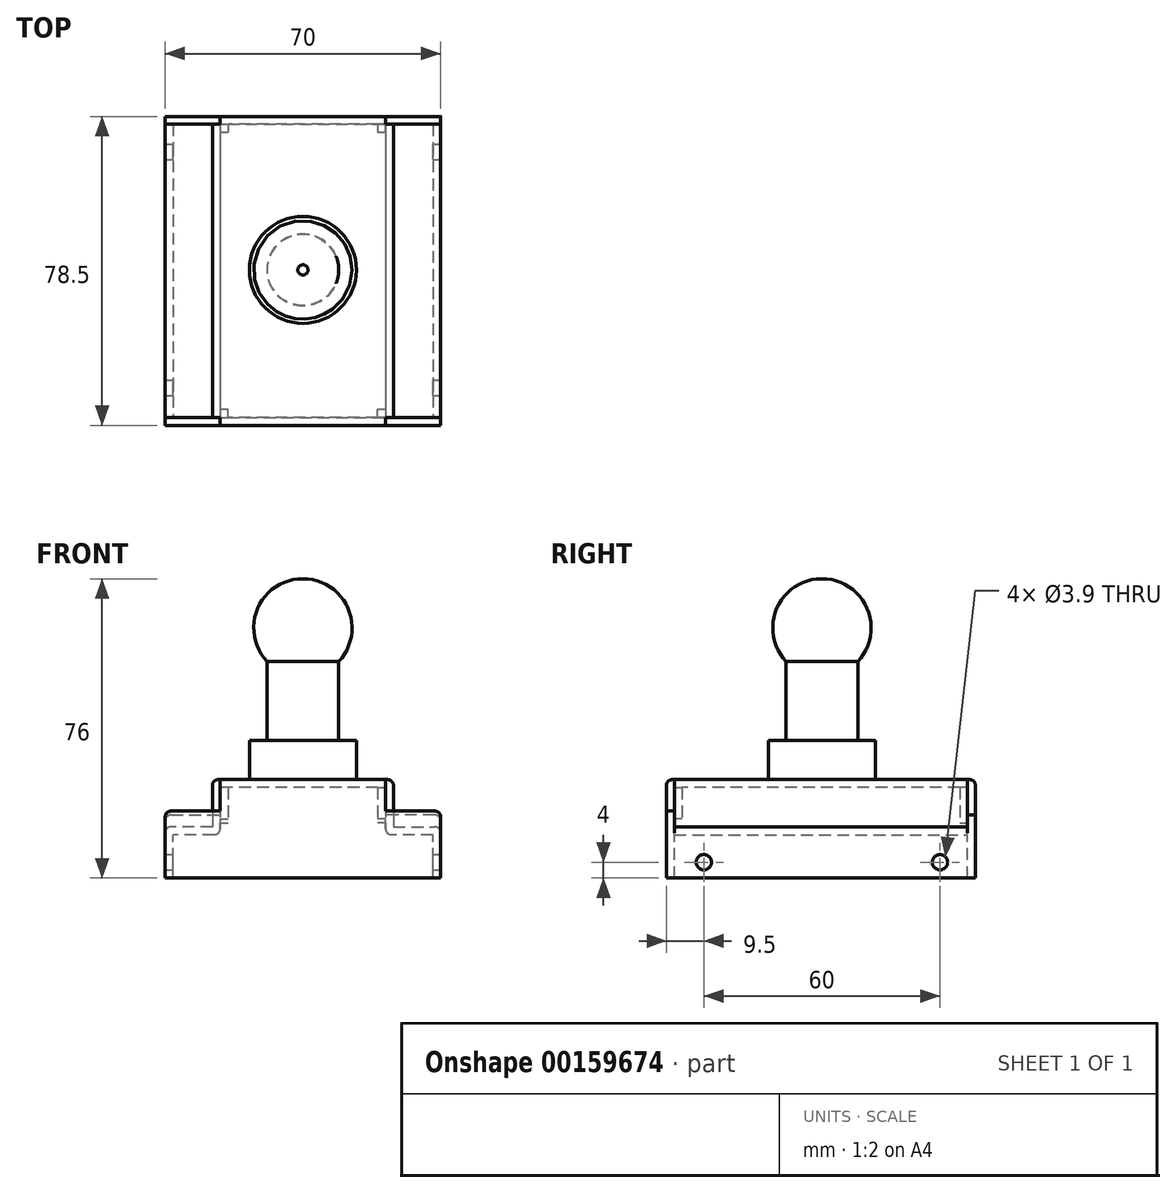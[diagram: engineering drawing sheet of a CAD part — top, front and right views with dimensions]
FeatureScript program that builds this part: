
annotation { "Feature Type Name" : "Feature", "Feature Type Description" : "" }
export const myFeature = defineFeature(function(context is Context, id is Id, definition is map)
    precondition{}
    {
        {
            var Q0;
            Q0=qCreatedBy(makeId("Front.planeOp"),FACE);
            cPlane(context, id + "F0", {"entities" : qUnion([Q0]), "cplaneType" : CPlaneType.OFFSET, "offset" : 39.5 * mm, "width" : 150 * mm, "height" : 150 * mm});
        }
        {
            var Q0;
            Q0=qCreatedBy(id+"F0.planeOp",FACE);
            var sketch = newSketch(context, id + "F1", { "sketchPlane" : qUnion([Q0])});
            skLineSegment(sketch, "E0.bottom", {"start": v(-35, 0) * mm, "end": v(35, 0) * mm});
            skLineSegment(sketch, "E0.top", {"start": v(-35, 25) * mm, "end": v(35, 25) * mm});
            skLineSegment(sketch, "E0.left", {"start": v(-35, 0) * mm, "end": v(-35, 25) * mm});
            skLineSegment(sketch, "E0.right", {"start": v(35, 0) * mm, "end": v(35, 25) * mm});
            skSolve(sketch);
        }
        {
            var Q0;
            Q0 = qSketchRegion(id + "F1", true);
            extrude(context, id + "F2", {"entities" : qUnion([Q0]), "oppositeDirection" : true, "depth" : 78.5 * mm});
        }
        {
            var Q0;
            Q0=makeQuery(id+"F2.opExtrude","CAP_FACE",FACE,{"disambiguationData":[OSD([sQuery(id+"F1.wireOp",EDGE,"E0.bottom"),sQuery(id+"F1.wireOp",EDGE,"E0.top"),sQuery(id+"F1.wireOp",EDGE,"E0.left"),sQuery(id+"F1.wireOp",EDGE,"E0.right")])],"isStart":true});
            var sketch = newSketch(context, id + "F3", { "sketchPlane" : qUnion([Q0])});
            skLineSegment(sketch, "E1.bottom", {"start": v(-36, 27) * mm, "end": v(-21, 27) * mm});
            skLineSegment(sketch, "E1.top", {"start": v(-36, 17) * mm, "end": v(-21, 17) * mm});
            skLineSegment(sketch, "E1.left", {"start": v(-36, 27) * mm, "end": v(-36, 17) * mm});
            skLineSegment(sketch, "E1.right", {"start": v(-21, 27) * mm, "end": v(-21, 17) * mm});
            skLineSegment(sketch, "E2.MirrorCS", {"start": v(36, 27) * mm, "end": v(21, 27) * mm});
            skLineSegment(sketch, "E3.MirrorCS", {"start": v(21, 27) * mm, "end": v(21, 17) * mm});
            skLineSegment(sketch, "E4.MirrorCS", {"start": v(36, 17) * mm, "end": v(21, 17) * mm});
            skLineSegment(sketch, "E5.MirrorCS", {"start": v(36, 27) * mm, "end": v(36, 17) * mm});
            skSolve(sketch);
        }
        {
            var Q0;
            Q0 = qSketchRegion(id + "F3", true);
            extrude(context, id + "F4", {"entities" : qUnion([Q0]), "operationType" : NewBodyOperationType.REMOVE, "oppositeDirection" : true, "depth" : 2 * mm});
        }
        {
            var Q0;
            Q0=makeQuery(id+"F2.opExtrude","CAP_FACE",FACE,{"disambiguationData":[OSD([sQuery(id+"F1.wireOp",EDGE,"E0.bottom"),sQuery(id+"F1.wireOp",EDGE,"E0.top"),sQuery(id+"F1.wireOp",EDGE,"E0.left"),sQuery(id+"F1.wireOp",EDGE,"E0.right")])],"isStart":false});
            var sketch = newSketch(context, id + "F5", { "sketchPlane" : qUnion([Q0])});
            skLineSegment(sketch, "E6.bottom", {"start": v(-36, 26) * mm, "end": v(-21, 26) * mm});
            skLineSegment(sketch, "E6.top", {"start": v(-36, 16) * mm, "end": v(-21, 16) * mm});
            skLineSegment(sketch, "E6.left", {"start": v(-36, 26) * mm, "end": v(-36, 16) * mm});
            skLineSegment(sketch, "E6.right", {"start": v(-21, 26) * mm, "end": v(-21, 16) * mm});
            skLineSegment(sketch, "E7.MirrorCS", {"start": v(36, 26) * mm, "end": v(21, 26) * mm});
            skLineSegment(sketch, "E8.MirrorCS", {"start": v(36, 16) * mm, "end": v(21, 16) * mm});
            skLineSegment(sketch, "E9.MirrorCS", {"start": v(21, 26) * mm, "end": v(21, 16) * mm});
            skLineSegment(sketch, "E10.MirrorCS", {"start": v(36, 26) * mm, "end": v(36, 16) * mm});
            skSolve(sketch);
        }
        {
            var Q0;
            Q0 = qSketchRegion(id + "F5", true);
            extrude(context, id + "F6", {"entities" : qUnion([Q0]), "operationType" : NewBodyOperationType.REMOVE, "oppositeDirection" : true, "depth" : 2 * mm});
        }
        {
            var Q0;
            Q0=makeQuery(id+"F4.boolean.opBoolean","COPY",FACE,{"derivedFrom":makeQuery(id+"F4.opExtrude","CAP_FACE",FACE,{"disambiguationData":[OSD([sQuery(id+"F3.wireOp",EDGE,"E2.MirrorCS"),sQuery(id+"F3.wireOp",EDGE,"E3.MirrorCS"),sQuery(id+"F3.wireOp",EDGE,"E4.MirrorCS"),sQuery(id+"F3.wireOp",EDGE,"E5.MirrorCS")])],"isStart":false})});
            var sketch = newSketch(context, id + "F7", { "sketchPlane" : qUnion([Q0])});
            skLineSegment(sketch, "E11.bottom", {"start": v(-23, 32.24) * mm, "end": v(-40.46, 32.24) * mm});
            skLineSegment(sketch, "E11.top", {"start": v(-23, 13) * mm, "end": v(-40.46, 13) * mm});
            skLineSegment(sketch, "E11.left", {"start": v(-23, 32.24) * mm, "end": v(-23, 13) * mm});
            skLineSegment(sketch, "E11.right", {"start": v(-40.46, 32.24) * mm, "end": v(-40.46, 13) * mm});
            skLineSegment(sketch, "E12.MirrorCS", {"start": v(23, 32.24) * mm, "end": v(23, 13) * mm});
            skLineSegment(sketch, "E13.MirrorCS", {"start": v(23, 32.24) * mm, "end": v(40.46, 32.24) * mm});
            skLineSegment(sketch, "E14.MirrorCS", {"start": v(40.46, 32.24) * mm, "end": v(40.46, 13) * mm});
            skLineSegment(sketch, "E15.MirrorCS", {"start": v(23, 13) * mm, "end": v(40.46, 13) * mm});
            skSolve(sketch);
        }
        {
            var Q0;
            Q0 = qSketchRegion(id + "F7", true);
            extrude(context, id + "F8", {"entities" : qUnion([Q0]), "operationType" : NewBodyOperationType.REMOVE, "oppositeDirection" : true, "depth" : 74.5 * mm});
        }
        {
            var Q0;
            Q0=makeQuery(id+"F2.opExtrude","CAP_EDGE",EDGE,{"disambiguationData":[OSD([sQuery(id+"F1.wireOp",EDGE,"E0.top")])],"isStart":true});
            var Q1;
            Q1=makeQuery(id+"F8.boolean.opBoolean","INTERSECT",EDGE,{"derivedFrom":[makeQuery(id+"F2.opExtrude","SWEPT_FACE",FACE,{"disambiguationData":[OSD([sQuery(id+"F1.wireOp",EDGE,"E0.top")])]}),makeQuery(id+"F8.opExtrude","SWEPT_FACE",FACE,{"disambiguationData":[OSD([sQuery(id+"F7.wireOp",EDGE,"E12.MirrorCS")])]})]});
            var Q2;
            Q2=makeQuery(id+"F2.opExtrude","CAP_EDGE",EDGE,{"disambiguationData":[OSD([sQuery(id+"F1.wireOp",EDGE,"E0.top")])],"isStart":false});
            var Q3;
            Q3=makeQuery(id+"F8.boolean.opBoolean","INTERSECT",EDGE,{"derivedFrom":[makeQuery(id+"F2.opExtrude","SWEPT_FACE",FACE,{"disambiguationData":[OSD([sQuery(id+"F1.wireOp",EDGE,"E0.top")])]}),makeQuery(id+"F8.opExtrude","SWEPT_FACE",FACE,{"disambiguationData":[OSD([sQuery(id+"F7.wireOp",EDGE,"E11.left")])]})]});
            var Q4;
            Q4=makeQuery(id+"F6.boolean.opBoolean","INTERSECT",EDGE,{"derivedFrom":[makeQuery(id+"F2.opExtrude","SWEPT_FACE",FACE,{"disambiguationData":[OSD([sQuery(id+"F1.wireOp",EDGE,"E0.left")])]}),makeQuery(id+"F6.opExtrude","SWEPT_FACE",FACE,{"disambiguationData":[OSD([sQuery(id+"F5.wireOp",EDGE,"E8.MirrorCS")])]})]});
            var Q5;
            Q5=makeQuery(id+"F6.boolean.opBoolean","INTERSECT",EDGE,{"derivedFrom":[makeQuery(id+"F2.opExtrude","SWEPT_FACE",FACE,{"disambiguationData":[OSD([sQuery(id+"F1.wireOp",EDGE,"E0.right")])]}),makeQuery(id+"F6.opExtrude","SWEPT_FACE",FACE,{"disambiguationData":[OSD([sQuery(id+"F5.wireOp",EDGE,"E6.top")])]})]});
            var Q6;
            Q6=makeQuery(id+"F4.boolean.opBoolean","INTERSECT",EDGE,{"derivedFrom":[makeQuery(id+"F2.opExtrude","SWEPT_FACE",FACE,{"disambiguationData":[OSD([sQuery(id+"F1.wireOp",EDGE,"E0.right")])]}),makeQuery(id+"F4.opExtrude","SWEPT_FACE",FACE,{"disambiguationData":[OSD([sQuery(id+"F3.wireOp",EDGE,"E4.MirrorCS")])]})]});
            var Q7;
            Q7=makeQuery(id+"F4.boolean.opBoolean","INTERSECT",EDGE,{"derivedFrom":[makeQuery(id+"F2.opExtrude","SWEPT_FACE",FACE,{"disambiguationData":[OSD([sQuery(id+"F1.wireOp",EDGE,"E0.left")])]}),makeQuery(id+"F4.opExtrude","SWEPT_FACE",FACE,{"disambiguationData":[OSD([sQuery(id+"F3.wireOp",EDGE,"E1.top")])]})]});
            var Q8;
            Q8=makeQuery(id+"F8.boolean.opBoolean","INTERSECT",EDGE,{"derivedFrom":[makeQuery(id+"F2.opExtrude","SWEPT_FACE",FACE,{"disambiguationData":[OSD([sQuery(id+"F1.wireOp",EDGE,"E0.left")])]}),makeQuery(id+"F8.opExtrude","SWEPT_FACE",FACE,{"disambiguationData":[OSD([sQuery(id+"F7.wireOp",EDGE,"E11.top")])]})]});
            var Q9;
            Q9=makeQuery(id+"F8.boolean.opBoolean","INTERSECT",EDGE,{"derivedFrom":[makeQuery(id+"F2.opExtrude","SWEPT_FACE",FACE,{"disambiguationData":[OSD([sQuery(id+"F1.wireOp",EDGE,"E0.right")])]}),makeQuery(id+"F8.opExtrude","SWEPT_FACE",FACE,{"disambiguationData":[OSD([sQuery(id+"F7.wireOp",EDGE,"E15.MirrorCS")])]})]});
            fillet(context, id + "F9", {"entities" : qUnion([Q0, Q1, Q2, Q3, Q4, Q5, Q6, Q7, Q8, Q9]), "radius" : 1.5 * mm, "tangentPropagation" : true, "allowEdgeOverflow" : false});
        }
        {
            var Q0;
            Q0=makeQuery(id+"F2.opExtrude","SWEPT_FACE",FACE,{"disambiguationData":[OSD([sQuery(id+"F1.wireOp",EDGE,"E0.bottom")])]});
            shell(context, id + "F10", {"entities" : qUnion([Q0]), "thickness" : 2 * mm});
        }
        {
            var Q0;
            Q0=makeQuery(id+"F10.opShell","OFFSET_EDGE",EDGE,{"disambiguationData":[OSD([sQuery(id+"F7.wireOp",EDGE,"E12.MirrorCS"),sQuery(id+"F7.wireOp",EDGE,"E15.MirrorCS")])]});
            var Q1;
            Q1=makeQuery(id+"F10.opShell","OFFSET_EDGE",EDGE,{"disambiguationData":[OSD([sQuery(id+"F7.wireOp",EDGE,"E11.top"),sQuery(id+"F7.wireOp",EDGE,"E11.left")])]});
            fillet(context, id + "F11", {"entities" : qUnion([Q0, Q1]), "radius" : 1.5 * mm, "tangentPropagation" : true, "allowEdgeOverflow" : false});
        }
        {
            var Q0;
            Q0=makeQuery(id+"F2.opExtrude","SWEPT_FACE",FACE,{"disambiguationData":[OSD([sQuery(id+"F1.wireOp",EDGE,"E0.right")])]});
            var sketch = newSketch(context, id + "F12", { "sketchPlane" : qUnion([Q0])});
            skCircle(sketch, "E16", {"center": v(-30, 4) * mm, "radius": 1.95 * mm});
            skCircle(sketch, "E17.MirrorC", {"center": v(30, 4) * mm, "radius": 1.95 * mm});
            skSolve(sketch);
        }
        {
            var Q0;
            Q0 = qSketchRegion(id + "F12", true);
            extrude(context, id + "F13", {"entities" : qUnion([Q0]), "operationType" : NewBodyOperationType.REMOVE, "endBound" : BoundingType.THROUGH_ALL, "oppositeDirection" : true, "depth" : 25 * mm});
        }
        {
            var Q0;
            Q0=makeQuery(id+"F2.opExtrude","SWEPT_FACE",FACE,{"disambiguationData":[OSD([sQuery(id+"F1.wireOp",EDGE,"E0.top")])]});
            var sketch = newSketch(context, id + "F14", { "sketchPlane" : qUnion([Q0])});
            skCircle(sketch, "E18", {"center": v(0, 0) * mm, "radius": 13.6 * mm});
            skSolve(sketch);
        }
        {
            var Q0;
            Q0 = qSketchRegion(id + "F14", true);
            extrude(context, id + "F15", {"entities" : qUnion([Q0]), "operationType" : NewBodyOperationType.ADD, "depth" : 10 * mm});
        }
        {
            var Q0;
            Q0=makeQuery(id+"F15.opExtrude","CAP_FACE",FACE,{"disambiguationData":[OSD([sQuery(id+"F14.wireOp",EDGE,"E18")])],"isStart":false});
            var sketch = newSketch(context, id + "F16", { "sketchPlane" : qUnion([Q0])});
            skCircle(sketch, "E19", {"center": v(0, 0) * mm, "radius": 9.1 * mm});
            skSolve(sketch);
        }
        {
            var Q0;
            Q0 = qSketchRegion(id + "F16", true);
            extrude(context, id + "F17", {"entities" : qUnion([Q0]), "operationType" : NewBodyOperationType.ADD, "depth" : 20 * mm});
        }
        {
            var Q0;
            Q0=makeQuery(id+"F17.opExtrude","CAP_FACE",FACE,{"disambiguationData":[OSD([sQuery(id+"F16.wireOp",EDGE,"E19")])],"isStart":false});
            var sketch = newSketch(context, id + "F18", { "sketchPlane" : qUnion([Q0])});
            skCircle(sketch, "E20", {"center": v(0, 0) * mm, "radius": 12.5 * mm});
            skSolve(sketch);
        }
        {
            var Q0;
            Q0 = qSketchRegion(id + "F18", true);
            extrude(context, id + "F19", {"entities" : qUnion([Q0]), "operationType" : NewBodyOperationType.ADD, "depth" : 21 * mm});
        }
        {
            var Q0;
            Q0=qCreatedBy(makeId("Front.planeOp"),FACE);
            var sketch = newSketch(context, id + "F20", { "sketchPlane" : qUnion([Q0])});
            skArc(sketch, "E21", {"start": v(9.1, 55) * mm, "mid": v(11.47, 68.52) * mm, "end": v(0, 76.07) * mm});
            skPoint(sketch, "E21.first.point", {"position": v(-9.1, 55) * mm});
            skPoint(sketch, "E21.second.point", {"position": v(9.1, 55) * mm});
            skPoint(sketch, "E21.third.point", {"position": v(12.5, 63.58) * mm});
            skLineSegment(sketch, "E22", {"start": v(9.1, 55) * mm, "end": v(14.1, 55) * mm});
            skLineSegment(sketch, "E23", {"start": v(14.1, 55) * mm, "end": v(14.1, 76.98) * mm});
            skLineSegment(sketch, "E24", {"start": v(14.1, 76.98) * mm, "end": v(0, 76.98) * mm});
            skLineSegment(sketch, "E25", {"start": v(0, 76.98) * mm, "end": v(0, 76.07) * mm});
            skSolve(sketch);
        }
        {
            var Q0;
            Q0 = qSketchRegion(id + "F20", true);
            var Q1;
            Q1=sQuery(id+"F20.wireOp",EDGE,"E25");
            revolve(context, id + "F21", {"operationType" : NewBodyOperationType.REMOVE, "entities" : qUnion([Q0]), "axis" : qUnion([Q1]), "revolveType" : RevolveType.FULL, "oppositeDirection" : true});
        }
    });
